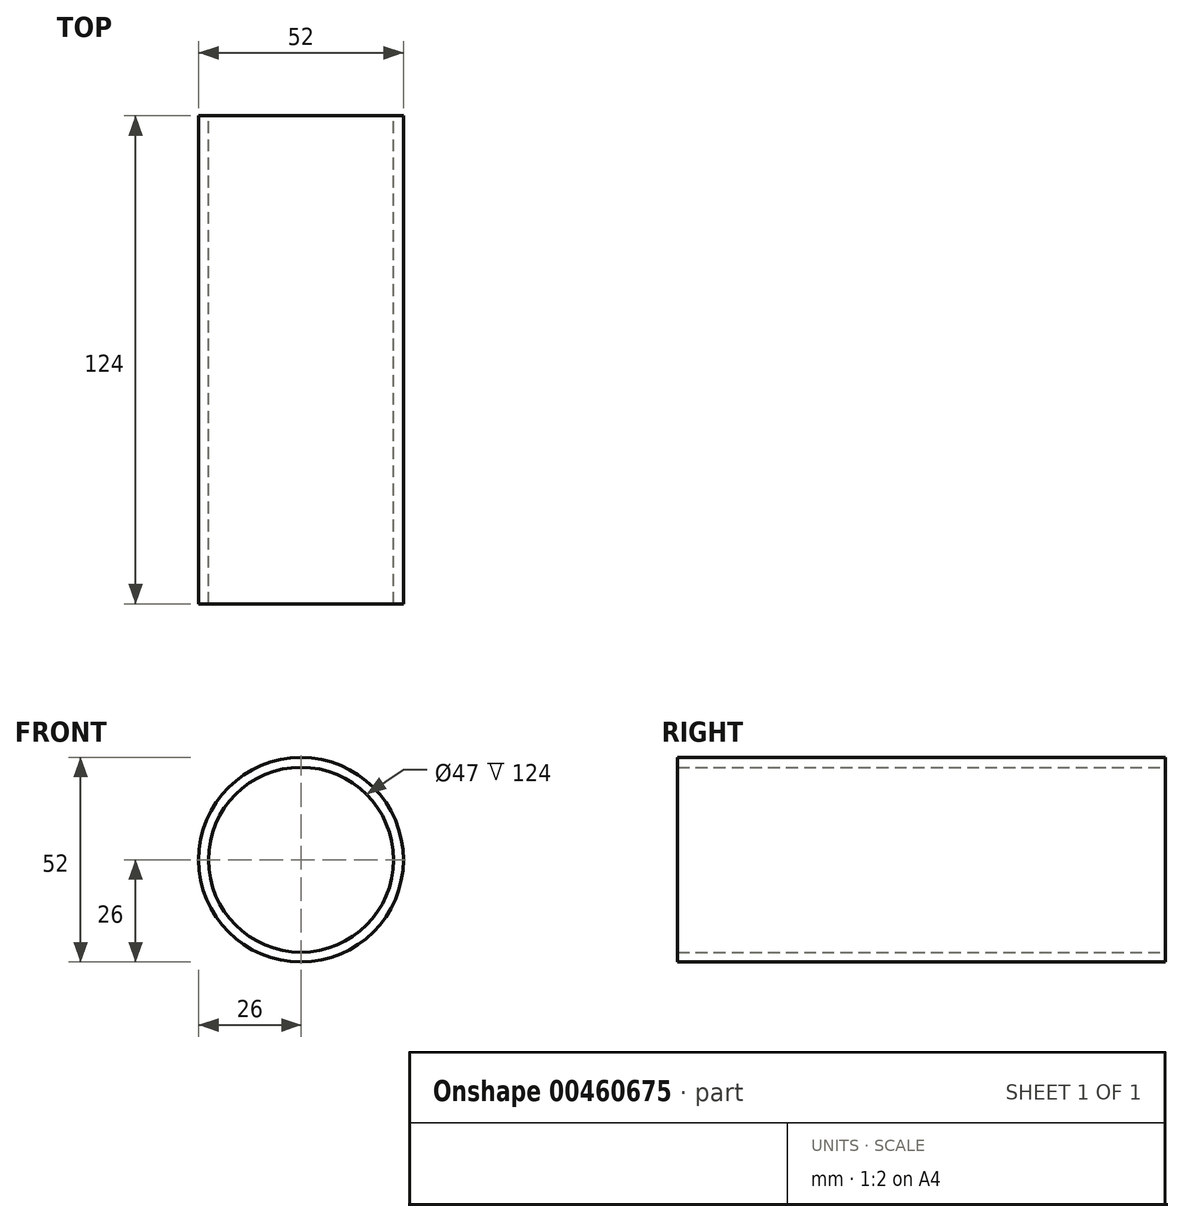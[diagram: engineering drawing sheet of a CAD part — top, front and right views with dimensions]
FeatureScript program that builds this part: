
annotation { "Feature Type Name" : "Feature", "Feature Type Description" : "" }
export const myFeature = defineFeature(function(context is Context, id is Id, definition is map)
    precondition{}
    {
        {
            var Q0;
            Q0=qCreatedBy(makeId("Front.planeOp"), FACE);
            var sketch = newSketch(context, id + "F0", { "sketchPlane" : qUnion([Q0])});
            skCircle(sketch, "E0", {"center": v(0, 0) * mm, "radius": 26 * mm});
            skCircle(sketch, "E1", {"center": v(0, 0) * mm, "radius": 23.5 * mm});
            skSolve(sketch);
        }
        {
            var Q0;
            Q0 = qSketchRegion(id + "F0", true);
            extrude(context, id + "F1", {"entities" : qUnion([Q0]), "depth" : 124 * mm, "offsetDistance" : 25 * mm});
        }
    });
